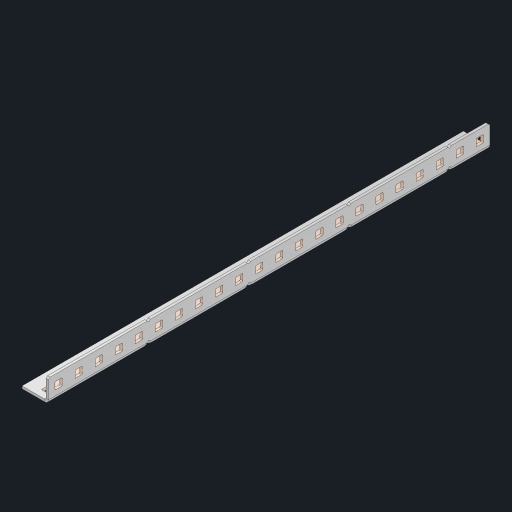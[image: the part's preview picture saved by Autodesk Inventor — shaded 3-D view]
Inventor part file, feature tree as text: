
AUTODESK INVENTOR PART (.ipt)
format: ipt  version: 2023 (Build 270158000, 158)  size: 813,568 bytes
history: native  units: in
note: dims shown in document units (in); Inventor stores cm internally (conversion verified against a paired STEP export)
features: other x49, extrude x43, sheet_metal_op x10, sketch x8, mirror x1, pattern_linear x1, chamfer x1
ambient origin geometry x8: Origin, YZ Plane, XZ Plane, XY Plane, X Axis, Y Axis, Z Axis, Center Point
bodies: Solid1 (feature_tree), Body (feature_tree)
feature tree (113):
  other  "Flange Pattern Plane"
  sheet_metal_op  "Flange Pattern"
  sheet_metal_op  "Body Pattern"
  other  "Arc Length"
  mirror  "Notch Mirror"
  pattern_linear  "Notch Pattern"  Spacing1=0.25in  [1 undecoded]
  chamfer  "End Chamfer"
  extrude  "Half Cut"  Depth=0.0625in
  sketch  "Sketch1"  dims[d0=1.5in]
  other  "Plate1"
  sketch  "Sketch2"  dims[d1=11.0in]
  other  "Plate2"
  sheet_metal_op  "Bend1"
  sheet_metal_op  "Corner1"
  sketch  "Sketch3"  dims[d2=0.0625in]
  other  "Flange Pattern Sketch"
  sketch  "Sketch7"  dims[d3=0.0625in]
  other  "Srf1"
  other  "Srf2"
  sketch  "Sketch8"  dims[d4=0.0312in]
  sketch  "Sketch9"  dims[d5=0.125in]
  other  "Srf91"
  sheet_metal_op  "Body Pattern Sketch"
  other  "Srf92"
  sketch  "Sketch13"  dims[d6=0.0625in]
  sketch  "Sketch14"  dims[d7=0.5in d8=90.0deg d9=0.0312in d10=0.25in d11=0.0625in d12=0.0625in d16=0.182in d17=0.02in d18=0.0625in d19=0.0in d20=0.25in d21=0.25in d46=0.172in d47=1.0in d48=0.0in d49=0.182in d50=0.02in d51=0.25in d52=0.25in d53=0.0625in d54=0.0in d55=0.172in d56=1.0in d57=0.0in d60=8.6614in d62=0.5in d63=0.3937in d65=0.5in d85=0.1473in d86=0.1782in d88=0.04in d89=0.0625in d90=0.0in d91=0.04in d92=0.0491in d95=2.5in d96=0.04in d97=0.25in d98=45.0deg d101=0.0in d102=2.497in d131=0.5in d132=8.6614in d134=0.5in d139=0.5in]
  other  "Srf856"
  other  "Srf1310"
  other  "Srf1311"
  other  "Srf1312"
  other  "Srf1376"
  other  "Srf1377"
  other  "Srf1728"
  other  "Srf1755"
  other  "Srf1878"
  other  "Srf1879"
  other  "Srf1880"
  other  "Srf1881"
  other  "Srf1882"
  other  "Srf1883"
  other  "Srf1884"
  other  "Srf1885"
  other  "Srf1886"
  other  "Srf1887"
  other  "Srf1888"
  other  "Srf1889"
  other  "Srf1890"
  other  "Srf1891"
  other  "Srf1892"
  other  "Srf1893"
  other  "Srf1942"
  other  "Srf1943"
  other  "Srf1944"
  other  "Srf1945"
  other  "Srf1946"
  other  "Srf1947"
  other  "Srf1948"
  other  "Srf1949"
  other  "Srf1950"
  other  "Srf1951"
  other  "Srf1952"
  other  "Srf1953"
  other  "Srf1954"
  other  "Srf1955"
  other  "Srf1956"
  other  "Srf1957"
  sheet_metal_op  "Flange Stamp"
  sheet_metal_op  "Flange Circle"
  sheet_metal_op  "Body Stamp"
  sheet_metal_op  "Body Circle"
  sheet_metal_op  "Notch"
  extrude  "ExtrusionSrf2"  Depth=0.0625in
  extrude  "ExtrusionSrf92"  Depth=0.5in
  extrude  "ExtrusionSrf856"  Depth=0.02in
  extrude  "ExtrusionSrf1310"  Depth=0.0625in
  extrude  "ExtrusionSrf1311"  TaperAngle=0.0deg  [1 undecoded]
  extrude  "ExtrusionSrf1312"  Depth=0.5in
  extrude  "ExtrusionSrf1376"  Depth=0.5in
  extrude  "ExtrusionSrf1377"  Depth=0.5in
  extrude  "ExtrusionSrf1728"  Depth=0.5in TaperAngle=0.0deg
  extrude  "ExtrusionSrf1755"  Depth=0.5in
  extrude  "ExtrusionSrf1878"  Depth=0.02in
  extrude  "ExtrusionSrf1879"  Depth=0.5in
  extrude  "ExtrusionSrf1880"  Depth=0.5in
  extrude  "ExtrusionSrf1881"  Depth=0.0625in
  extrude  "ExtrusionSrf1882"  TaperAngle=0.0deg  [1 undecoded]
  extrude  "ExtrusionSrf1883"  Depth=0.5in
  extrude  "ExtrusionSrf1884"  Depth=0.5in TaperAngle=0.0deg
  extrude  "ExtrusionSrf1885"  Depth=0.5in
  extrude  "ExtrusionSrf1886"  Depth=0.5in
  extrude  "ExtrusionSrf1887"  Depth=0.5in
  extrude  "ExtrusionSrf1888"  Depth=0.5in
  extrude  "ExtrusionSrf1889"  Depth=0.5in
  extrude  "ExtrusionSrf1890"  Depth=0.0625in
  extrude  "ExtrusionSrf1891"  TaperAngle=0.0deg  [1 undecoded]
  extrude  "ExtrusionSrf1892"  Depth=0.5in
  extrude  "ExtrusionSrf1893"  Depth=0.5in
  extrude  "ExtrusionSrf1942"  Depth=0.5in
  extrude  "ExtrusionSrf1943"  Depth=0.5in TaperAngle=45.0deg
  extrude  "ExtrusionSrf1944"  TaperAngle=0.0deg  [1 undecoded]
  extrude  "ExtrusionSrf1945"  Depth=0.5in
  extrude  "ExtrusionSrf1946"  Depth=0.5in
  extrude  "ExtrusionSrf1947"  Depth=0.5in
  extrude  "ExtrusionSrf1948"  Depth=0.5in
  extrude  "ExtrusionSrf1949"  Depth=0.5in
  extrude  "ExtrusionSrf1950"  [1 undecoded]
  extrude  "ExtrusionSrf1951"  [1 undecoded]
  extrude  "ExtrusionSrf1952"  [1 undecoded]
  extrude  "ExtrusionSrf1953"  [1 undecoded]
  extrude  "ExtrusionSrf1954"  [1 undecoded]
  extrude  "ExtrusionSrf1955"  [1 undecoded]
  extrude  "ExtrusionSrf1956"  [1 undecoded]
  extrude  "ExtrusionSrf1957"  [1 undecoded]
note: 13 required parameter values undecoded (feature->parameter linkage not recoverable at this tier; creation-order binding heuristic only, values carry confidence <= 0.55)
